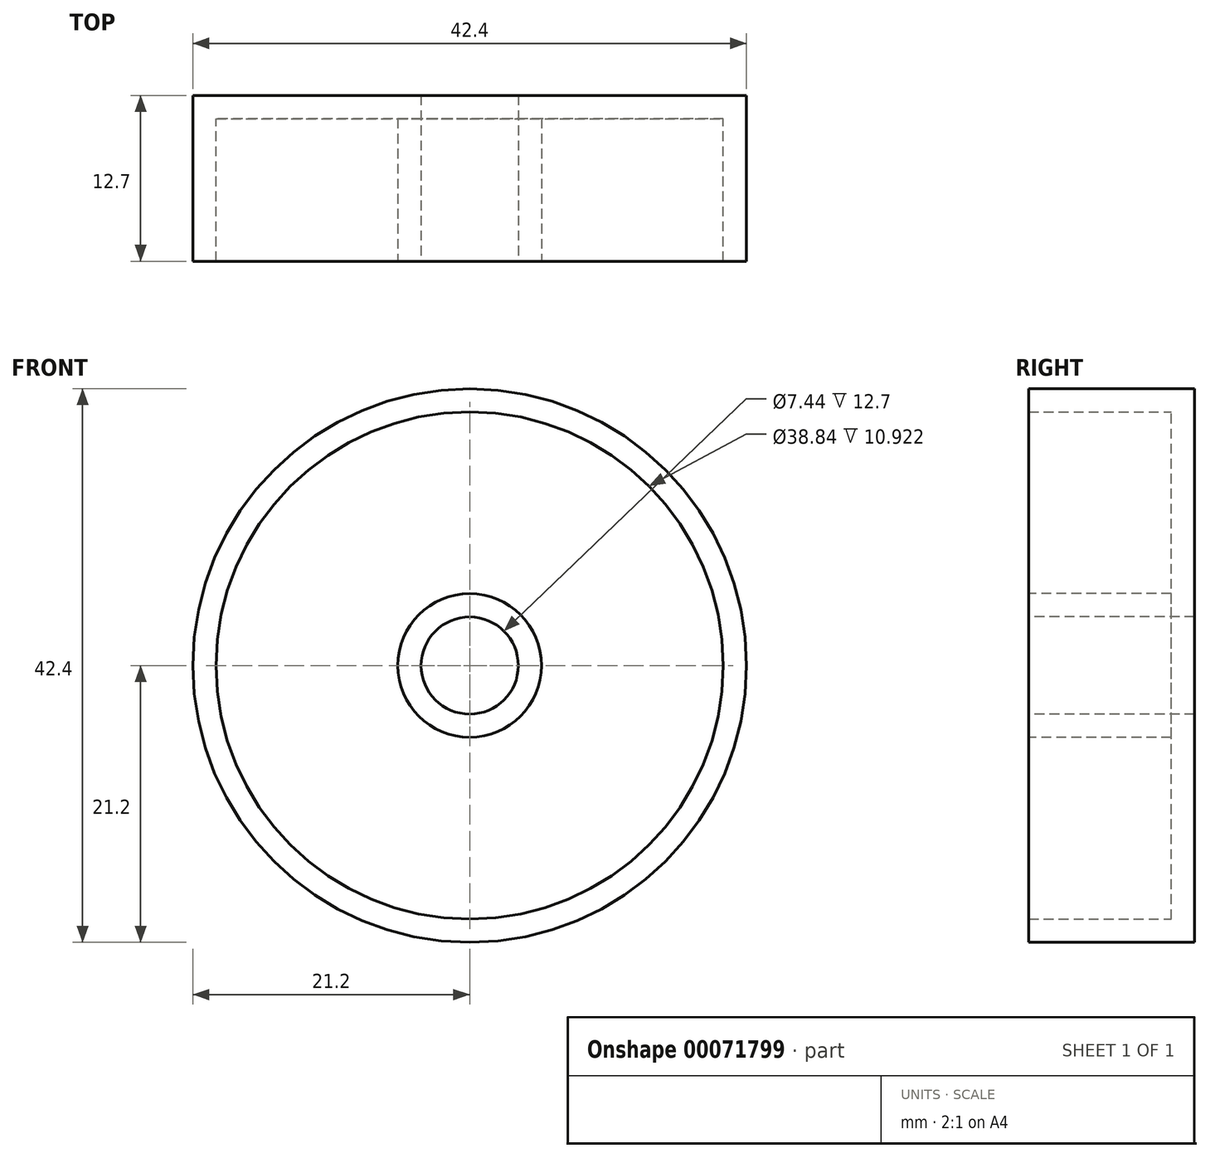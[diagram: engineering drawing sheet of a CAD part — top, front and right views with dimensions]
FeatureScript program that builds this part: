
annotation { "Feature Type Name" : "Feature", "Feature Type Description" : "" }
export const myFeature = defineFeature(function(context is Context, id is Id, definition is map)
    precondition{}
    {
        {
            var Q0;
            Q0=qCreatedBy(makeId("Front.planeOp"),FACE);
            var sketch = newSketch(context, id + "F0", { "sketchPlane" : qUnion([Q0])});
            skCircle(sketch, "E0", {"center": v(0, 0) * mm, "radius": 21.2 * mm});
            skSolve(sketch);
        }
        {
            var Q0;
            Q0 = qSketchRegion(id + "F0", true);
            extrude(context, id + "F1", {"entities" : qUnion([Q0]), "depth" : 12.7 * mm});
        }
        {
            var Q0;
            Q0=makeQuery(id+"F1.opExtrude","CAP_FACE",FACE,{"disambiguationData":[OSD([sQuery(id+"F0.wireOp",EDGE,"E0")])],"isStart":false});
            var sketch = newSketch(context, id + "F2", { "sketchPlane" : qUnion([Q0])});
            skCircle(sketch, "E1", {"center": v(0, 0) * mm, "radius": 3.72 * mm});
            skSolve(sketch);
        }
        {
            var Q0;
            Q0 = qSketchRegion(id + "F2", true);
            extrude(context, id + "F3", {"entities" : qUnion([Q0]), "operationType" : NewBodyOperationType.REMOVE, "endBound" : BoundingType.THROUGH_ALL, "oppositeDirection" : true, "depth" : 25.4 * mm});
        }
        {
            var Q0;
            Q0=makeQuery(id+"F1.opExtrude","CAP_FACE",FACE,{"disambiguationData":[OSD([sQuery(id+"F0.wireOp",EDGE,"E0")])],"isStart":false});
            shell(context, id + "F4", {"entities" : qUnion([Q0]), "thickness" : 1.78 * mm});
        }
    });
